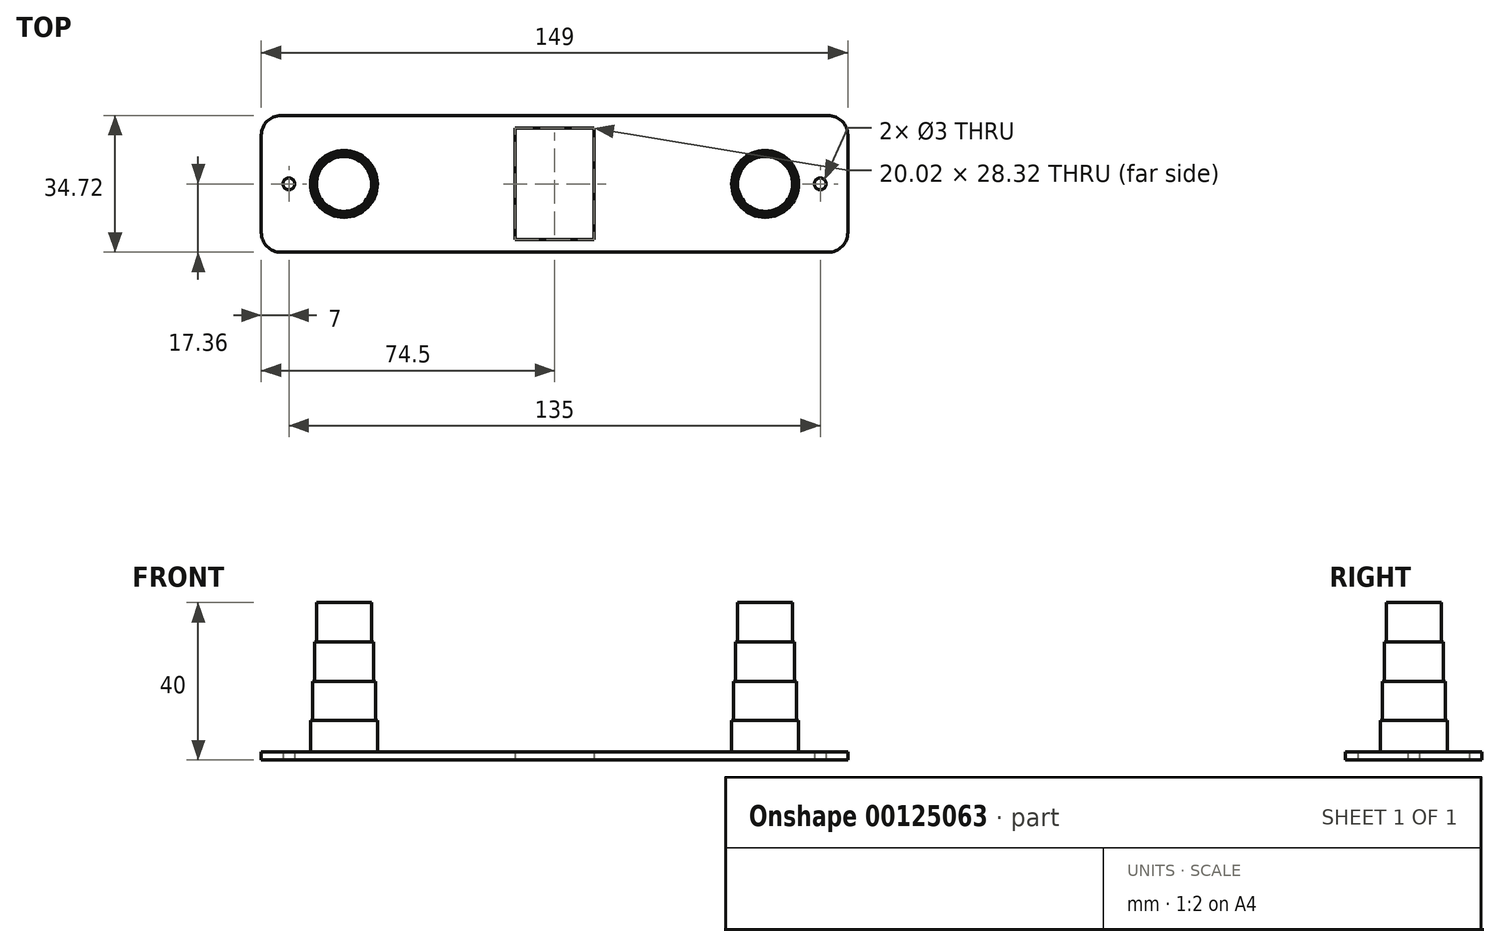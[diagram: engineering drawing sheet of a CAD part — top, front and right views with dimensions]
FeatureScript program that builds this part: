
annotation { "Feature Type Name" : "Feature", "Feature Type Description" : "" }
export const myFeature = defineFeature(function(context is Context, id is Id, definition is map)
    precondition{}
    {
        {
            var Q0;
            Q0=qCreatedBy(makeId("Top.planeOp"),FACE);
            var sketch = newSketch(context, id + "F0", { "sketchPlane" : qUnion([Q0])});
            skCircle(sketch, "E0", {"center": v(-53.5, 0) * mm, "radius": 7 * mm});
            skCircle(sketch, "E1", {"center": v(53.5, 0) * mm, "radius": 7 * mm});
            skLineSegment(sketch, "E2.bottom", {"start": v(-69.5, 17.36) * mm, "end": v(69.5, 17.36) * mm});
            skLineSegment(sketch, "E2.top", {"start": v(-69.5, -17.36) * mm, "end": v(69.5, -17.36) * mm});
            skLineSegment(sketch, "E2.left", {"start": v(-74.5, 12.36) * mm, "end": v(-74.5, -12.36) * mm});
            skLineSegment(sketch, "E2.right", {"start": v(74.5, 12.36) * mm, "end": v(74.5, -12.36) * mm});
            skPoint(sketch, "E2.middle", {"position": v(0, 0) * mm});
            skPoint(sketch, "E3.visualSharp", {"position": v(-74.5, 17.36) * mm});
            skArc(sketch, "E3.filletArc", {"start": v(-69.5, 17.36) * mm, "mid": v(-73.04, 15.9) * mm, "end": v(-74.5, 12.36) * mm});
            skPoint(sketch, "E4.visualSharp", {"position": v(74.5, 17.36) * mm});
            skArc(sketch, "E4.filletArc", {"start": v(74.5, 12.36) * mm, "mid": v(73.04, 15.9) * mm, "end": v(69.5, 17.36) * mm});
            skPoint(sketch, "E5.visualSharp", {"position": v(74.5, -17.36) * mm});
            skArc(sketch, "E5.filletArc", {"start": v(69.5, -17.36) * mm, "mid": v(73.04, -15.9) * mm, "end": v(74.5, -12.36) * mm});
            skPoint(sketch, "E6.visualSharp", {"position": v(-74.5, -17.36) * mm});
            skArc(sketch, "E6.filletArc", {"start": v(-74.5, -12.36) * mm, "mid": v(-73.04, -15.9) * mm, "end": v(-69.5, -17.36) * mm});
            skCircle(sketch, "E7", {"center": v(-67.5, 0) * mm, "radius": 1.5 * mm});
            skCircle(sketch, "E8", {"center": v(67.5, 0) * mm, "radius": 1.5 * mm});
            skLineSegment(sketch, "E9.bottom", {"start": v(-53.5, 4) * mm, "end": v(53.5, 4) * mm});
            skLineSegment(sketch, "E9.top", {"start": v(-53.5, -4) * mm, "end": v(53.5, -4) * mm});
            skLineSegment(sketch, "E9.left", {"start": v(-53.5, 4) * mm, "end": v(-53.5, -4) * mm});
            skLineSegment(sketch, "E9.right", {"start": v(53.5, 4) * mm, "end": v(53.5, -4) * mm});
            skLineSegment(sketch, "E10.bottom", {"start": v(10.01, 14.16) * mm, "end": v(-10.01, 14.16) * mm});
            skLineSegment(sketch, "E10.top", {"start": v(10.01, -14.16) * mm, "end": v(-10.01, -14.16) * mm});
            skLineSegment(sketch, "E10.left", {"start": v(10.01, 14.16) * mm, "end": v(10.01, -14.16) * mm});
            skLineSegment(sketch, "E10.right", {"start": v(-10.01, 14.16) * mm, "end": v(-10.01, -14.16) * mm});
            skCircle(sketch, "E11", {"center": v(-53.5, 0) * mm, "radius": 7.5 * mm});
            skCircle(sketch, "E12", {"center": v(-53.5, 0) * mm, "radius": 8 * mm});
            skCircle(sketch, "E13", {"center": v(-53.5, 0) * mm, "radius": 8.5 * mm});
            skCircle(sketch, "E14", {"center": v(53.5, 0) * mm, "radius": 7.5 * mm});
            skCircle(sketch, "E15", {"center": v(53.5, 0) * mm, "radius": 8 * mm});
            skCircle(sketch, "E16", {"center": v(53.5, 0) * mm, "radius": 8.5 * mm});
            skSolve(sketch);
        }
        {
            var Q0;
            Q0=makeQuery(id+"F0.imprint","IMPRINT",FACE,{"disambiguationData":[TD([[makeQuery(id+"F0.imprint","IMPRINT",EDGE,{"derivedFrom":sQuery(id+"F0.wireOp",EDGE,"E2.bottom")}),-1.0]])]});
            var Q1;
            {var subQ0=sQuery(id+"F0.wireOp",EDGE,"E13");var subQ1=sQuery(id+"F0.wireOp",EDGE,"E9.bottom");var subQ2=makeQuery(id+"F0.imprint","INTERSECT",VERTEX,{"derivedFrom":[subQ1,subQ0]});Q1=makeQuery(id+"F0.imprint","IMPRINT",FACE,{"disambiguationData":[TD([[makeQuery(id+"F0.imprint","IMPRINT",EDGE,{"disambiguationData":[TD([[subQ2,-1.0]])],"derivedFrom":subQ1}),-1.0]])]});}
            var Q2;
            {var subQ0=sQuery(id+"F0.wireOp",EDGE,"E10.left");var subQ1=sQuery(id+"F0.wireOp",EDGE,"E9.bottom");var subQ2=makeQuery(id+"F0.imprint","INTERSECT",VERTEX,{"derivedFrom":[subQ1,subQ0]});Q2=makeQuery(id+"F0.imprint","IMPRINT",FACE,{"disambiguationData":[TD([[makeQuery(id+"F0.imprint","IMPRINT",EDGE,{"disambiguationData":[TD([[subQ2,-1.0]])],"derivedFrom":subQ1}),-1.0]])]});}
            var Q3;
            {var subQ5=sQuery(id+"F0.wireOp",EDGE,"E9.left");Q3=makeQuery(id+"F0.imprint","IMPRINT",FACE,{"disambiguationData":[TD([[makeQuery(id+"F0.imprint","IMPRINT",EDGE,{"derivedFrom":subQ5}),1.0]])]});}
            var Q4;
            {var subQ5=sQuery(id+"F0.wireOp",EDGE,"E9.left");Q4=makeQuery(id+"F0.imprint","IMPRINT",FACE,{"disambiguationData":[TD([[makeQuery(id+"F0.imprint","IMPRINT",EDGE,{"derivedFrom":subQ5}),-1.0]])]});}
            var Q5;
            {var subQ0=sQuery(id+"F0.wireOp",EDGE,"E9.bottom");var subQ1=sQuery(id+"F0.wireOp",EDGE,"E0");var subQ2=makeQuery(id+"F0.imprint","INTERSECT",VERTEX,{"derivedFrom":[subQ1,subQ0]});Q5=makeQuery(id+"F0.imprint","IMPRINT",FACE,{"disambiguationData":[TD([[makeQuery(id+"F0.imprint","IMPRINT",EDGE,{"disambiguationData":[TD([[subQ2,-1.0]])],"derivedFrom":subQ1}),-1.0]])]});}
            var Q6;
            {var subQ0=sQuery(id+"F0.wireOp",EDGE,"E11");var subQ1=sQuery(id+"F0.wireOp",EDGE,"E9.bottom");var subQ2=makeQuery(id+"F0.imprint","INTERSECT",VERTEX,{"derivedFrom":[subQ1,subQ0]});Q6=makeQuery(id+"F0.imprint","IMPRINT",FACE,{"disambiguationData":[TD([[makeQuery(id+"F0.imprint","IMPRINT",EDGE,{"disambiguationData":[TD([[subQ2,-1.0]])],"derivedFrom":subQ1}),1.0]])]});}
            var Q7;
            {var subQ0=sQuery(id+"F0.wireOp",EDGE,"E12");var subQ1=sQuery(id+"F0.wireOp",EDGE,"E9.bottom");var subQ2=makeQuery(id+"F0.imprint","INTERSECT",VERTEX,{"derivedFrom":[subQ1,subQ0]});Q7=makeQuery(id+"F0.imprint","IMPRINT",FACE,{"disambiguationData":[TD([[makeQuery(id+"F0.imprint","IMPRINT",EDGE,{"disambiguationData":[TD([[subQ2,-1.0]])],"derivedFrom":subQ1}),1.0]])]});}
            var Q8;
            {var subQ0=sQuery(id+"F0.wireOp",EDGE,"E9.bottom");var subQ1=sQuery(id+"F0.wireOp",EDGE,"E0");var subQ2=makeQuery(id+"F0.imprint","INTERSECT",VERTEX,{"derivedFrom":[subQ1,subQ0]});Q8=makeQuery(id+"F0.imprint","IMPRINT",FACE,{"disambiguationData":[TD([[makeQuery(id+"F0.imprint","IMPRINT",EDGE,{"disambiguationData":[TD([[subQ2,1.0]])],"derivedFrom":subQ1}),-1.0]])]});}
            var Q9;
            {var subQ0=sQuery(id+"F0.wireOp",EDGE,"E11");var subQ1=sQuery(id+"F0.wireOp",EDGE,"E9.bottom");var subQ2=makeQuery(id+"F0.imprint","INTERSECT",VERTEX,{"derivedFrom":[subQ1,subQ0]});Q9=makeQuery(id+"F0.imprint","IMPRINT",FACE,{"disambiguationData":[TD([[makeQuery(id+"F0.imprint","IMPRINT",EDGE,{"disambiguationData":[TD([[subQ2,-1.0]])],"derivedFrom":subQ1}),-1.0]])]});}
            var Q10;
            {var subQ0=sQuery(id+"F0.wireOp",EDGE,"E12");var subQ1=sQuery(id+"F0.wireOp",EDGE,"E9.bottom");var subQ2=makeQuery(id+"F0.imprint","INTERSECT",VERTEX,{"derivedFrom":[subQ1,subQ0]});Q10=makeQuery(id+"F0.imprint","IMPRINT",FACE,{"disambiguationData":[TD([[makeQuery(id+"F0.imprint","IMPRINT",EDGE,{"disambiguationData":[TD([[subQ2,-1.0]])],"derivedFrom":subQ1}),-1.0]])]});}
            var Q11;
            {var subQ5=sQuery(id+"F0.wireOp",EDGE,"E9.right");Q11=makeQuery(id+"F0.imprint","IMPRINT",FACE,{"disambiguationData":[TD([[makeQuery(id+"F0.imprint","IMPRINT",EDGE,{"derivedFrom":subQ5}),1.0]])]});}
            var Q12;
            {var subQ5=sQuery(id+"F0.wireOp",EDGE,"E9.right");Q12=makeQuery(id+"F0.imprint","IMPRINT",FACE,{"disambiguationData":[TD([[makeQuery(id+"F0.imprint","IMPRINT",EDGE,{"derivedFrom":subQ5}),-1.0]])]});}
            var Q13;
            {var subQ0=sQuery(id+"F0.wireOp",EDGE,"E9.bottom");var subQ1=sQuery(id+"F0.wireOp",EDGE,"E1");var subQ2=makeQuery(id+"F0.imprint","INTERSECT",VERTEX,{"derivedFrom":[subQ1,subQ0]});Q13=makeQuery(id+"F0.imprint","IMPRINT",FACE,{"disambiguationData":[TD([[makeQuery(id+"F0.imprint","IMPRINT",EDGE,{"disambiguationData":[TD([[subQ2,-1.0]])],"derivedFrom":subQ1}),-1.0]])]});}
            var Q14;
            {var subQ0=sQuery(id+"F0.wireOp",EDGE,"E15");var subQ1=sQuery(id+"F0.wireOp",EDGE,"E9.bottom");var subQ2=makeQuery(id+"F0.imprint","INTERSECT",VERTEX,{"derivedFrom":[subQ1,subQ0]});Q14=makeQuery(id+"F0.imprint","IMPRINT",FACE,{"disambiguationData":[TD([[makeQuery(id+"F0.imprint","IMPRINT",EDGE,{"disambiguationData":[TD([[subQ2,-1.0]])],"derivedFrom":subQ1}),-1.0]])]});}
            var Q15;
            {var subQ0=sQuery(id+"F0.wireOp",EDGE,"E16");var subQ1=sQuery(id+"F0.wireOp",EDGE,"E9.bottom");var subQ2=makeQuery(id+"F0.imprint","INTERSECT",VERTEX,{"derivedFrom":[subQ1,subQ0]});Q15=makeQuery(id+"F0.imprint","IMPRINT",FACE,{"disambiguationData":[TD([[makeQuery(id+"F0.imprint","IMPRINT",EDGE,{"disambiguationData":[TD([[subQ2,-1.0]])],"derivedFrom":subQ1}),-1.0]])]});}
            var Q16;
            {var subQ0=sQuery(id+"F0.wireOp",EDGE,"E16");var subQ1=sQuery(id+"F0.wireOp",EDGE,"E9.bottom");var subQ2=makeQuery(id+"F0.imprint","INTERSECT",VERTEX,{"derivedFrom":[subQ1,subQ0]});Q16=makeQuery(id+"F0.imprint","IMPRINT",FACE,{"disambiguationData":[TD([[makeQuery(id+"F0.imprint","IMPRINT",EDGE,{"disambiguationData":[TD([[subQ2,-1.0]])],"derivedFrom":subQ1}),1.0]])]});}
            var Q17;
            {var subQ0=sQuery(id+"F0.wireOp",EDGE,"E15");var subQ1=sQuery(id+"F0.wireOp",EDGE,"E9.bottom");var subQ2=makeQuery(id+"F0.imprint","INTERSECT",VERTEX,{"derivedFrom":[subQ1,subQ0]});Q17=makeQuery(id+"F0.imprint","IMPRINT",FACE,{"disambiguationData":[TD([[makeQuery(id+"F0.imprint","IMPRINT",EDGE,{"disambiguationData":[TD([[subQ2,-1.0]])],"derivedFrom":subQ1}),1.0]])]});}
            var Q18;
            {var subQ0=sQuery(id+"F0.wireOp",EDGE,"E9.bottom");var subQ1=sQuery(id+"F0.wireOp",EDGE,"E1");var subQ2=makeQuery(id+"F0.imprint","INTERSECT",VERTEX,{"derivedFrom":[subQ1,subQ0]});Q18=makeQuery(id+"F0.imprint","IMPRINT",FACE,{"disambiguationData":[TD([[makeQuery(id+"F0.imprint","IMPRINT",EDGE,{"disambiguationData":[TD([[subQ2,1.0]])],"derivedFrom":subQ1}),-1.0]])]});}
            extrude(context, id + "F1", {"entities" : qUnion([Q0, Q1, Q2, Q3, Q4, Q5, Q6, Q7, Q8, Q9, Q10, Q11, Q12, Q13, Q14, Q15, Q16, Q17, Q18]), "depth" : 2 * mm});
        }
        {
            var Q0;
            {var subQ5=sQuery(id+"F0.wireOp",EDGE,"E9.left");Q0=makeQuery(id+"F0.imprint","IMPRINT",FACE,{"disambiguationData":[TD([[makeQuery(id+"F0.imprint","IMPRINT",EDGE,{"derivedFrom":subQ5}),-1.0]])]});}
            var Q1;
            {var subQ5=sQuery(id+"F0.wireOp",EDGE,"E9.left");Q1=makeQuery(id+"F0.imprint","IMPRINT",FACE,{"disambiguationData":[TD([[makeQuery(id+"F0.imprint","IMPRINT",EDGE,{"derivedFrom":subQ5}),1.0]])]});}
            var Q2;
            {var subQ5=sQuery(id+"F0.wireOp",EDGE,"E9.right");Q2=makeQuery(id+"F0.imprint","IMPRINT",FACE,{"disambiguationData":[TD([[makeQuery(id+"F0.imprint","IMPRINT",EDGE,{"derivedFrom":subQ5}),-1.0]])]});}
            var Q3;
            {var subQ5=sQuery(id+"F0.wireOp",EDGE,"E9.right");Q3=makeQuery(id+"F0.imprint","IMPRINT",FACE,{"disambiguationData":[TD([[makeQuery(id+"F0.imprint","IMPRINT",EDGE,{"derivedFrom":subQ5}),1.0]])]});}
            extrude(context, id + "F2", {"entities" : qUnion([Q0, Q1, Q2, Q3]), "operationType" : NewBodyOperationType.ADD, "depth" : 40 * mm});
        }
        {
            var Q0;
            {var subQ0=sQuery(id+"F0.wireOp",EDGE,"E9.bottom");var subQ1=sQuery(id+"F0.wireOp",EDGE,"E0");var subQ2=makeQuery(id+"F0.imprint","INTERSECT",VERTEX,{"derivedFrom":[subQ1,subQ0]});Q0=makeQuery(id+"F0.imprint","IMPRINT",FACE,{"disambiguationData":[TD([[makeQuery(id+"F0.imprint","IMPRINT",EDGE,{"disambiguationData":[TD([[subQ2,-1.0]])],"derivedFrom":subQ1}),-1.0]])]});}
            var Q1;
            {var subQ0=sQuery(id+"F0.wireOp",EDGE,"E9.bottom");var subQ1=sQuery(id+"F0.wireOp",EDGE,"E0");var subQ2=makeQuery(id+"F0.imprint","INTERSECT",VERTEX,{"derivedFrom":[subQ1,subQ0]});Q1=makeQuery(id+"F0.imprint","IMPRINT",FACE,{"disambiguationData":[TD([[makeQuery(id+"F0.imprint","IMPRINT",EDGE,{"disambiguationData":[TD([[subQ2,1.0]])],"derivedFrom":subQ1}),-1.0]])]});}
            var Q2;
            {var subQ0=sQuery(id+"F0.wireOp",EDGE,"E9.bottom");var subQ1=sQuery(id+"F0.wireOp",EDGE,"E1");var subQ2=makeQuery(id+"F0.imprint","INTERSECT",VERTEX,{"derivedFrom":[subQ1,subQ0]});Q2=makeQuery(id+"F0.imprint","IMPRINT",FACE,{"disambiguationData":[TD([[makeQuery(id+"F0.imprint","IMPRINT",EDGE,{"disambiguationData":[TD([[subQ2,-1.0]])],"derivedFrom":subQ1}),-1.0]])]});}
            var Q3;
            {var subQ0=sQuery(id+"F0.wireOp",EDGE,"E9.bottom");var subQ1=sQuery(id+"F0.wireOp",EDGE,"E1");var subQ2=makeQuery(id+"F0.imprint","INTERSECT",VERTEX,{"derivedFrom":[subQ1,subQ0]});Q3=makeQuery(id+"F0.imprint","IMPRINT",FACE,{"disambiguationData":[TD([[makeQuery(id+"F0.imprint","IMPRINT",EDGE,{"disambiguationData":[TD([[subQ2,1.0]])],"derivedFrom":subQ1}),-1.0]])]});}
            extrude(context, id + "F3", {"entities" : qUnion([Q0, Q1, Q2, Q3]), "operationType" : NewBodyOperationType.ADD, "depth" : 30 * mm});
        }
        {
            var Q0;
            {var subQ0=sQuery(id+"F0.wireOp",EDGE,"E11");var subQ1=sQuery(id+"F0.wireOp",EDGE,"E9.bottom");var subQ2=makeQuery(id+"F0.imprint","INTERSECT",VERTEX,{"derivedFrom":[subQ1,subQ0]});Q0=makeQuery(id+"F0.imprint","IMPRINT",FACE,{"disambiguationData":[TD([[makeQuery(id+"F0.imprint","IMPRINT",EDGE,{"disambiguationData":[TD([[subQ2,-1.0]])],"derivedFrom":subQ1}),1.0]])]});}
            var Q1;
            {var subQ0=sQuery(id+"F0.wireOp",EDGE,"E11");var subQ1=sQuery(id+"F0.wireOp",EDGE,"E9.bottom");var subQ2=makeQuery(id+"F0.imprint","INTERSECT",VERTEX,{"derivedFrom":[subQ1,subQ0]});Q1=makeQuery(id+"F0.imprint","IMPRINT",FACE,{"disambiguationData":[TD([[makeQuery(id+"F0.imprint","IMPRINT",EDGE,{"disambiguationData":[TD([[subQ2,-1.0]])],"derivedFrom":subQ1}),-1.0]])]});}
            var Q2;
            {var subQ0=sQuery(id+"F0.wireOp",EDGE,"E15");var subQ1=sQuery(id+"F0.wireOp",EDGE,"E9.bottom");var subQ2=makeQuery(id+"F0.imprint","INTERSECT",VERTEX,{"derivedFrom":[subQ1,subQ0]});Q2=makeQuery(id+"F0.imprint","IMPRINT",FACE,{"disambiguationData":[TD([[makeQuery(id+"F0.imprint","IMPRINT",EDGE,{"disambiguationData":[TD([[subQ2,-1.0]])],"derivedFrom":subQ1}),-1.0]])]});}
            var Q3;
            {var subQ0=sQuery(id+"F0.wireOp",EDGE,"E15");var subQ1=sQuery(id+"F0.wireOp",EDGE,"E9.bottom");var subQ2=makeQuery(id+"F0.imprint","INTERSECT",VERTEX,{"derivedFrom":[subQ1,subQ0]});Q3=makeQuery(id+"F0.imprint","IMPRINT",FACE,{"disambiguationData":[TD([[makeQuery(id+"F0.imprint","IMPRINT",EDGE,{"disambiguationData":[TD([[subQ2,-1.0]])],"derivedFrom":subQ1}),1.0]])]});}
            extrude(context, id + "F4", {"entities" : qUnion([Q0, Q1, Q2, Q3]), "operationType" : NewBodyOperationType.ADD, "depth" : 20 * mm});
        }
        {
            var Q0;
            {var subQ0=sQuery(id+"F0.wireOp",EDGE,"E16");var subQ1=sQuery(id+"F0.wireOp",EDGE,"E9.bottom");var subQ2=makeQuery(id+"F0.imprint","INTERSECT",VERTEX,{"derivedFrom":[subQ1,subQ0]});Q0=makeQuery(id+"F0.imprint","IMPRINT",FACE,{"disambiguationData":[TD([[makeQuery(id+"F0.imprint","IMPRINT",EDGE,{"disambiguationData":[TD([[subQ2,-1.0]])],"derivedFrom":subQ1}),-1.0]])]});}
            var Q1;
            {var subQ0=sQuery(id+"F0.wireOp",EDGE,"E16");var subQ1=sQuery(id+"F0.wireOp",EDGE,"E9.bottom");var subQ2=makeQuery(id+"F0.imprint","INTERSECT",VERTEX,{"derivedFrom":[subQ1,subQ0]});Q1=makeQuery(id+"F0.imprint","IMPRINT",FACE,{"disambiguationData":[TD([[makeQuery(id+"F0.imprint","IMPRINT",EDGE,{"disambiguationData":[TD([[subQ2,-1.0]])],"derivedFrom":subQ1}),1.0]])]});}
            var Q2;
            {var subQ0=sQuery(id+"F0.wireOp",EDGE,"E12");var subQ1=sQuery(id+"F0.wireOp",EDGE,"E9.bottom");var subQ2=makeQuery(id+"F0.imprint","INTERSECT",VERTEX,{"derivedFrom":[subQ1,subQ0]});Q2=makeQuery(id+"F0.imprint","IMPRINT",FACE,{"disambiguationData":[TD([[makeQuery(id+"F0.imprint","IMPRINT",EDGE,{"disambiguationData":[TD([[subQ2,-1.0]])],"derivedFrom":subQ1}),-1.0]])]});}
            var Q3;
            {var subQ0=sQuery(id+"F0.wireOp",EDGE,"E12");var subQ1=sQuery(id+"F0.wireOp",EDGE,"E9.bottom");var subQ2=makeQuery(id+"F0.imprint","INTERSECT",VERTEX,{"derivedFrom":[subQ1,subQ0]});Q3=makeQuery(id+"F0.imprint","IMPRINT",FACE,{"disambiguationData":[TD([[makeQuery(id+"F0.imprint","IMPRINT",EDGE,{"disambiguationData":[TD([[subQ2,-1.0]])],"derivedFrom":subQ1}),1.0]])]});}
            extrude(context, id + "F5", {"entities" : qUnion([Q0, Q1, Q2, Q3]), "operationType" : NewBodyOperationType.ADD, "depth" : 10 * mm});
        }
    });
